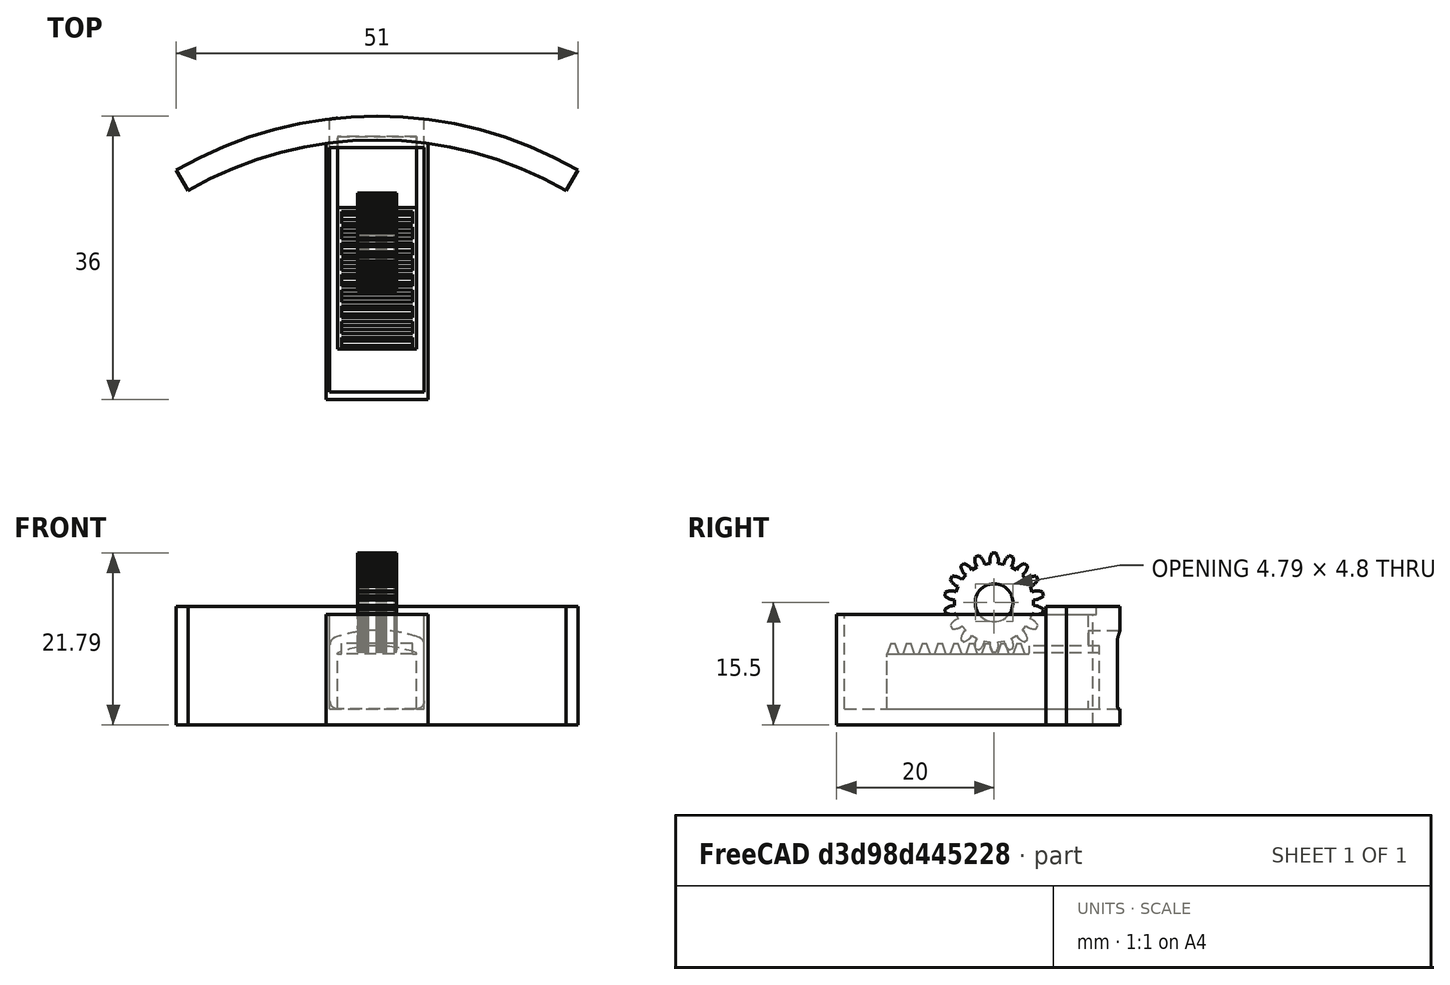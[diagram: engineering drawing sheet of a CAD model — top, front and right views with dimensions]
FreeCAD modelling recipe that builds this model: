
FCSTD DOCUMENT  (FreeCAD 0.16R4924 (Git))
Label: interior_servo_bay_v4p9
License: All rights reserved
LicenseURL: http://en.wikipedia.org/wiki/All_rights_reserved
objects: Part::Feature×11, Part::Cut×5, Part::Box×5, Part::MultiFuse×4, Part::Cylinder×3, Part::Extrusion×3, Part::Thickness×1, Mesh::Feature×1, Part::Fuse×1, Part::FeaturePython×1, Part::Prism×1, Part::MultiCommon×1
note: 36 computed .brp shape members not serialized (recipe doc carries the construction recipe); baked Part::Feature solids carry a one-line shape summary decoded from their .brp

FEATURE [Part::Cylinder] Cylinder  label="bottle_wall"
  Angle = 60
  Height = 15
  Placement = pos=(8.5,-7,0) rot=(0,0,1;1.0472rad)
  Radius = 51
FEATURE [Part::Cylinder] Cylinder001  label="bottle_wall001"
  Angle = 60
  Height = 15
  Placement = pos=(8.5,-7,0) rot=(0,0,1;1.0472rad)
  Radius = 48
FEATURE [Part::Cut] Cut  label="bottle_wall_composite"
  Base = -> Cylinder
  Placement = pos=(0,-2,0) rot=(0,0,1;0rad)
  Tool = -> Cylinder001
FEATURE [Part::Feature] Common_cs  label="pin_cs"
  Placement = pos=(3.5,35,2) rot=(0,0,1;0rad)
  shape: bbox 10 x 2e-07 x 8 mm, 0 faces, 0 solids (baked)
FEATURE [Part::Extrusion] Extrude
  Base = -> Common_cs
  Dir = (0,5,0)
  Solid = true
FEATURE [Part::Thickness] Thickness
  Faces = -> Extrude [Face7]
  Intersection = false
  Join = 0
  Mode = 0
  SelfIntersection = false
  Value = 1
FEATURE [Part::Feature] Common_cs001  label="pin_cs001"
  Placement = pos=(3.5,35,2) rot=(0,0,1;0rad)
  shape: bbox 10 x 2e-07 x 8 mm, 0 faces, 0 solids (baked)
FEATURE [Part::Extrusion] Extrude001
  Base = -> Common_cs001
  Dir = (0,5,0)
  Solid = true
FEATURE [Part::MultiFuse] Fusion  label="bolt_bottle_side_opening"
  Placement = pos=(0,-7,1) rot=(0,0,1;0rad)
  Shapes = -> [Thickness,Extrude,Extrude001]
FEATURE [Part::Box] Box  label="pullBay"
  Height = 15
  Length = 12
  Placement = pos=(2.5,7,2) rot=(0,0,1;0rad)
  Width = 31
FEATURE [Part::Box] Box001  label="Case"
  Height = 14
  Length = 13
  Placement = pos=(2,6,0) rot=(0,0,1;0rad)
  Width = 34
FEATURE [Part::Cut] Cut001  label="cut bay from case"
  Base = -> Box001
  Tool = -> Box
FEATURE [Part::MultiFuse] Fusion001  label="wall plus case"
  Shapes = -> [Cut,Cut001]
FEATURE [Part::Cut] Cut002  label="hole cut out of case"
  Base = -> Fusion001
  Tool = -> Fusion
FEATURE [Mesh::Feature] Mesh  label="servo_motor_2"
  Placement = pos=(33.6,-52,22) rot=(0,0,-1;1.5708rad)
FEATURE [Part::Fuse] union  label="pinion"
FEATURE [Part::FeaturePython] RefineLinearExtrude  # WARN: FeaturePython — macro-defined, semantics opaque (R4)
  Base = -> union
FEATURE [Part::Extrusion] LinearExtrude
  Base = -> RefineLinearExtrude
  Dir = (0,0,5)
  Solid = true
FEATURE [Part::Prism] prism
  Circumradius = 2.4
  Height = 7
  Placement = pos=(0,0,-1) rot=(0,0,1;0rad)
  Polygon = 50
FEATURE [Part::Cut] difference  label="pinion_final"
  Base = -> LinearExtrude
  Placement = pos=(6,26,15.5) rot=(0,1,0;1.5708rad)
  Tool = -> prism
FEATURE [Part::Cylinder] Cylinder002  label="rounded_top"
  Angle = 360
  Height = 40
  Placement = pos=(5,35,-7) rot=(1,0,0;1.5708rad)
  Radius = 15
FEATURE [Part::Box] Box005  label="pin"
  Height = 8
  Length = 10
  Width = 27
FEATURE [Part::MultiCommon] Common  label="rounded pin"
  Shapes = -> [Cylinder002,Box005]
FEATURE [Part::Box] Box006  label="flat_top"
  Height = 10
  Length = 10
  Placement = pos=(0,0,7) rot=(0,0,1;0rad)
  Width = 18
FEATURE [Part::Cut] Cut005
  Base = -> Common
  Placement = pos=(0,11,0) rot=(0,0,1;0rad)
  Tool = -> Box006
FEATURE [Part::Box] cube
  Height = 5
  Length = 18
  Placement = pos=(-12,-4.5,-2.5) rot=(0,0,1;0rad)
  Width = 9
FEATURE [Part::Feature] polyhedron
  Placement = pos=(-11.2451,0,2.5) rot=(0,0,1;0rad)
  shape: bbox 1.51 x 9 x 1.337 mm, 6 faces (baked)
FEATURE [Part::Feature] polyhedron001
  Placement = pos=(-9.24512,0,2.5) rot=(0,0,1;0rad)
  shape: bbox 1.51 x 9 x 1.337 mm, 6 faces (baked)
FEATURE [Part::Feature] polyhedron002
  Placement = pos=(-7.24512,0,2.5) rot=(0,0,1;0rad)
  shape: bbox 1.51 x 9 x 1.337 mm, 6 faces (baked)
FEATURE [Part::Feature] polyhedron003
  Placement = pos=(-5.24512,0,2.5) rot=(0,0,1;0rad)
  shape: bbox 1.51 x 9 x 1.337 mm, 6 faces (baked)
FEATURE [Part::Feature] polyhedron004
  Placement = pos=(-3.24512,0,2.5) rot=(0,0,1;0rad)
  shape: bbox 1.51 x 9 x 1.337 mm, 6 faces (baked)
FEATURE [Part::Feature] polyhedron005
  Placement = pos=(-1.24512,0,2.5) rot=(0,0,1;0rad)
  shape: bbox 1.51 x 9 x 1.337 mm, 6 faces (baked)
FEATURE [Part::Feature] polyhedron006
  Placement = pos=(0.754882,0,2.5) rot=(0,0,1;0rad)
  shape: bbox 1.51 x 9 x 1.337 mm, 6 faces (baked)
FEATURE [Part::Feature] polyhedron007
  Placement = pos=(2.75488,0,2.5) rot=(0,0,1;0rad)
  shape: bbox 1.51 x 9 x 1.337 mm, 6 faces (baked)
FEATURE [Part::Feature] polyhedron008
  Placement = pos=(4.75488,0,2.5) rot=(0,0,1;0rad)
  shape: bbox 1.51 x 9 x 1.337 mm, 6 faces (baked)
FEATURE [Part::MultiFuse] Fusion003  label="rack"
  Placement = pos=(5,23,4.5) rot=(0,0,1;1.5708rad)
  Shapes = -> [cube,polyhedron002,polyhedron003,polyhedron004,polyhedron005,polyhedron,polyhedron007,polyhedron001,polyhedron006,polyhedron008]
FEATURE [Part::MultiFuse] Fusion004  label="pin_3p2"
  Placement = pos=(3.5,1.4,2) rot=(0,0,1;0rad)
  Shapes = -> [Fusion003,Cut005]
